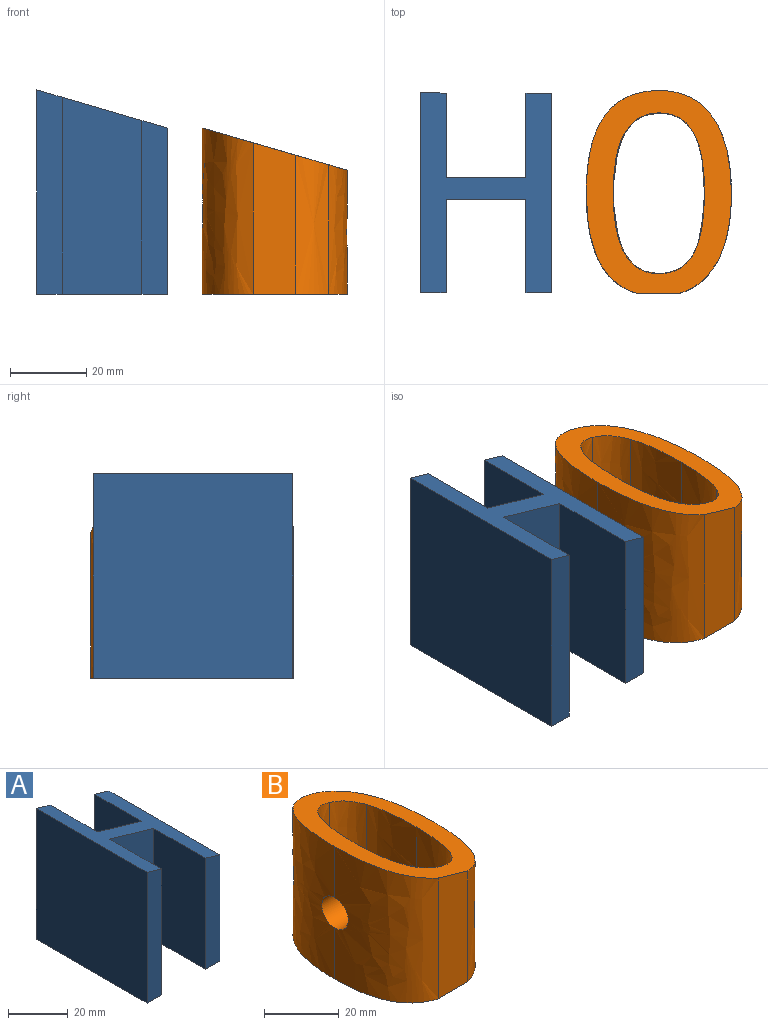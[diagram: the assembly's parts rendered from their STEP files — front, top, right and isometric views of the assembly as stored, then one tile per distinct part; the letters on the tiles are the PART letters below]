
ASSEMBLY  parts=2 mates=1
PART A: 17 faces, bbox 34.3x52.2x53.5 mm
  f0: plane 53.5x6.68mm, normal (0,-1,0), area 350.8mm2, adj f3,f11,f12,f14
  f1: plane 45.45x6.69mm, normal (0,-1,0), area 297.5mm2, adj f4,f10,f12,f14
  f2: plane 51.55x22.01mm, normal (1,0,0), area 1134.7mm2, adj f7,f8,f12,f14
  f3: plane 51.55x24.37mm, normal (1,0,0), area 1256.2mm2, adj f0,f9,f12,f14
  f4: plane 52.25x43.5mm, normal (1,0,0), area 2194.1mm2, adj f1,f5,f13,f14,f15
  f5: plane 45.45x6.69mm, normal (0,1,0), area 297.5mm2, adj f4,f6,f12,f14
  f6: plane 45.45x22.01mm, normal (-1,0,0), area 1000.5mm2, adj f5,f7,f12,f14
  f7: plane 51.55x20.9mm, normal (0,1,0), area 1013.8mm2, adj f2,f6,f12,f14
  f8: plane 53.5x6.68mm, normal (0,1,0), area 350.8mm2, adj f2,f11,f12,f14
  f9: plane 51.55x20.9mm, normal (0,-1,0), area 1013.8mm2, adj f3,f10,f12,f14
  f10: plane 45.45x24.37mm, normal (-1,0,0), area 1107.6mm2, adj f1,f9,f12,f14
  f11: plane 53.5x52.25mm, normal (-1,0,0), area 2795.1mm2, adj f0,f8,f12,f14
  f12: plane 52.25x34.27mm, normal (0.28,0,0.96), area 855.2mm2, adj f0,f1,f2,f3,f5,f6,f7,f8
  f13: plane 52.25x0mm, normal (0,0,1), area 0mm2, adj f4,f12
  f14: plane 52.25x34.27mm, normal (0,0,-1), area 821mm2, adj f0,f1,f2,f3,f4,f5,f6,f7
  f15: cylinder r=5mm len=10mm, axis (1,0,0), area 125.7mm2, adj f4,f16
  f16: plane 10x10mm, normal (1,0,0), area 78.5mm2, adj f15
PART B: 18 faces, bbox 38x53.8x43.5 mm
  f0: extruded ~33.86x19.91mm, area 644.1mm2, adj f1,f8,f13,f15,f17
  f1: extruded ~33.84x19.89mm, area 644.1mm2, adj f0,f9,f13,f15,f17
  f2: extruded ~35.32x15.92mm, area 528.9mm2, adj f3,f10,f13,f15,f17
  f3: extruded ~35.31x15.91mm, area 526.5mm2, adj f2,f11,f13,f15,f17
  f4: extruded ~43.5x26.27mm, area 1306.3mm2, adj f5,f12,f13,f14,f15,f16
  f5: extruded ~43.5x26.8mm, area 1527.9mm2, adj f4,f9,f12,f13,f15,f16
  f6: extruded ~41.45x21.09mm, area 1062.3mm2, adj f7,f11,f13,f15,f16
  f7: extruded ~41.45x21.01mm, area 1062.7mm2, adj f6,f10,f13,f15,f16
  f8: extruded ~36.38x8.63mm, area 381.4mm2, adj f0,f13,f14,f15
  f9: extruded ~37.93x14.02mm, area 583.9mm2, adj f1,f5,f13,f15
  f10: extruded ~37.93x8.95mm, area 395.8mm2, adj f2,f7,f13,f15
  f11: extruded ~37.95x9.06mm, area 401.8mm2, adj f3,f6,f13,f15
  f12: plane 0.82x0mm, normal (0,0,1), area 0mm2, adj f4,f5,f13
  f13: plane 53.07x37.97mm, normal (0.28,0,0.96), area 880.3mm2, adj f0,f1,f2,f3,f4,f5,f6,f7
  f14: plane 39.62x11.12mm, normal (0,-1,0), area 422.4mm2, adj f4,f8,f13,f15
  f15: plane 53.79x37.98mm, normal (0,0,-1), area 845mm2, adj f0,f1,f2,f3,f4,f5,f6,f7
  f16: cylinder r=5mm len=10mm, axis (-1,0,0), area 221.1mm2, adj f4,f5,f6,f7
  f17: cylinder r=5mm len=10mm, axis (1,0,0), area 220.5mm2, adj f0,f1,f2,f3
PLACE A t=(-13.89,-45.17,12.08)mm
PLACE B t=(-12.62,-45.31,12.08)mm
MATE parallel B.f15 <-> A.f14  axis (0,0,-1) through (-70.63,-19.04,28.58)mm
